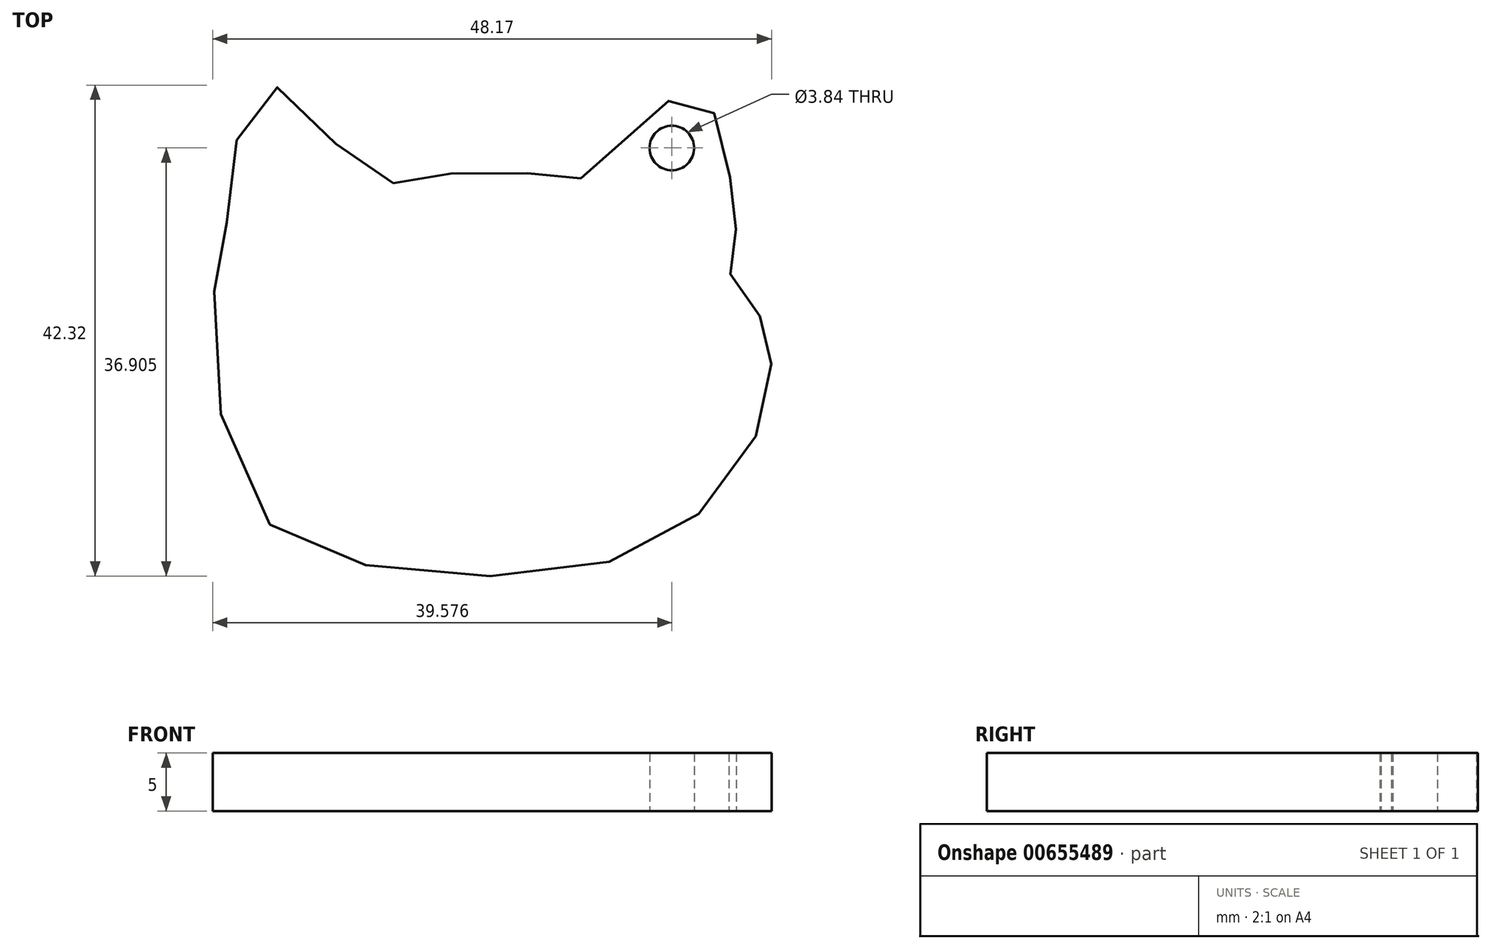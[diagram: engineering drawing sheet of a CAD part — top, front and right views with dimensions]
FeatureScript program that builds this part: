
annotation { "Feature Type Name" : "Feature", "Feature Type Description" : "" }
export const myFeature = defineFeature(function(context is Context, id is Id, definition is map)
    precondition{}
    {
        {
            var Q0;
            Q0=qCreatedBy(makeId("Top.planeOp"),FACE);
            var sketch = newSketch(context, id + "F0", { "sketchPlane" : qUnion([Q0])});
            skFitSpline(sketch, "E0", {"points": [v(26.68, 14.07) * mm, v(36.67, 22.1) * mm, v(38.37, 18.68) * mm, v(39.56, 14.16) * mm, v(39.86, 11.19) * mm, v(40, 8.15) * mm, v(39.49, 6.07) * mm, v(41.34, 3.7) * mm, v(42.38, 1.32) * mm, v(43.06, -1.28) * mm, v(42.45, -6.4) * mm, v(37.04, -14.7) * mm, v(26.06, -19.67) * mm, v(8.7, -19.38) * mm, v(-1.76, -13.74) * mm, v(-4.95, 3.77) * mm, v(-3.91, 9.48) * mm, v(-3.1, 16.75) * mm, v(0, 21.95) * mm, v(4.84, 17.87) * mm, v(9.92, 13.74) * mm, v(12.7, 14.03) * mm, v(18.38, 14.63) * mm, v(24.03, 14.13) * mm, v(26.68, 14.07) * mm]});
            skPoint(sketch, "E1.center.orphan", {"position": v(30.46, 6.07) * mm});
            skCircle(sketch, "E2", {"center": v(34.54, 16.67) * mm, "radius": 1.92 * mm});
            skSolve(sketch);
        }
        {
            var Q0;
            Q0 = qSketchRegion(id + "F0", true);
            extrude(context, id + "F1", {"entities" : qUnion([Q0]), "depth" : 5 * mm, "offsetDistance" : 25 * mm});
        }
        {
            var Q0;
            Q0 = qSketchRegion(id + "F0", true);
            extrude(context, id + "F2", {"entities" : qUnion([Q0]), "operationType" : NewBodyOperationType.REMOVE, "oppositeDirection" : true, "depth" : 5 * mm, "offsetDistance" : 25 * mm});
        }
    });
